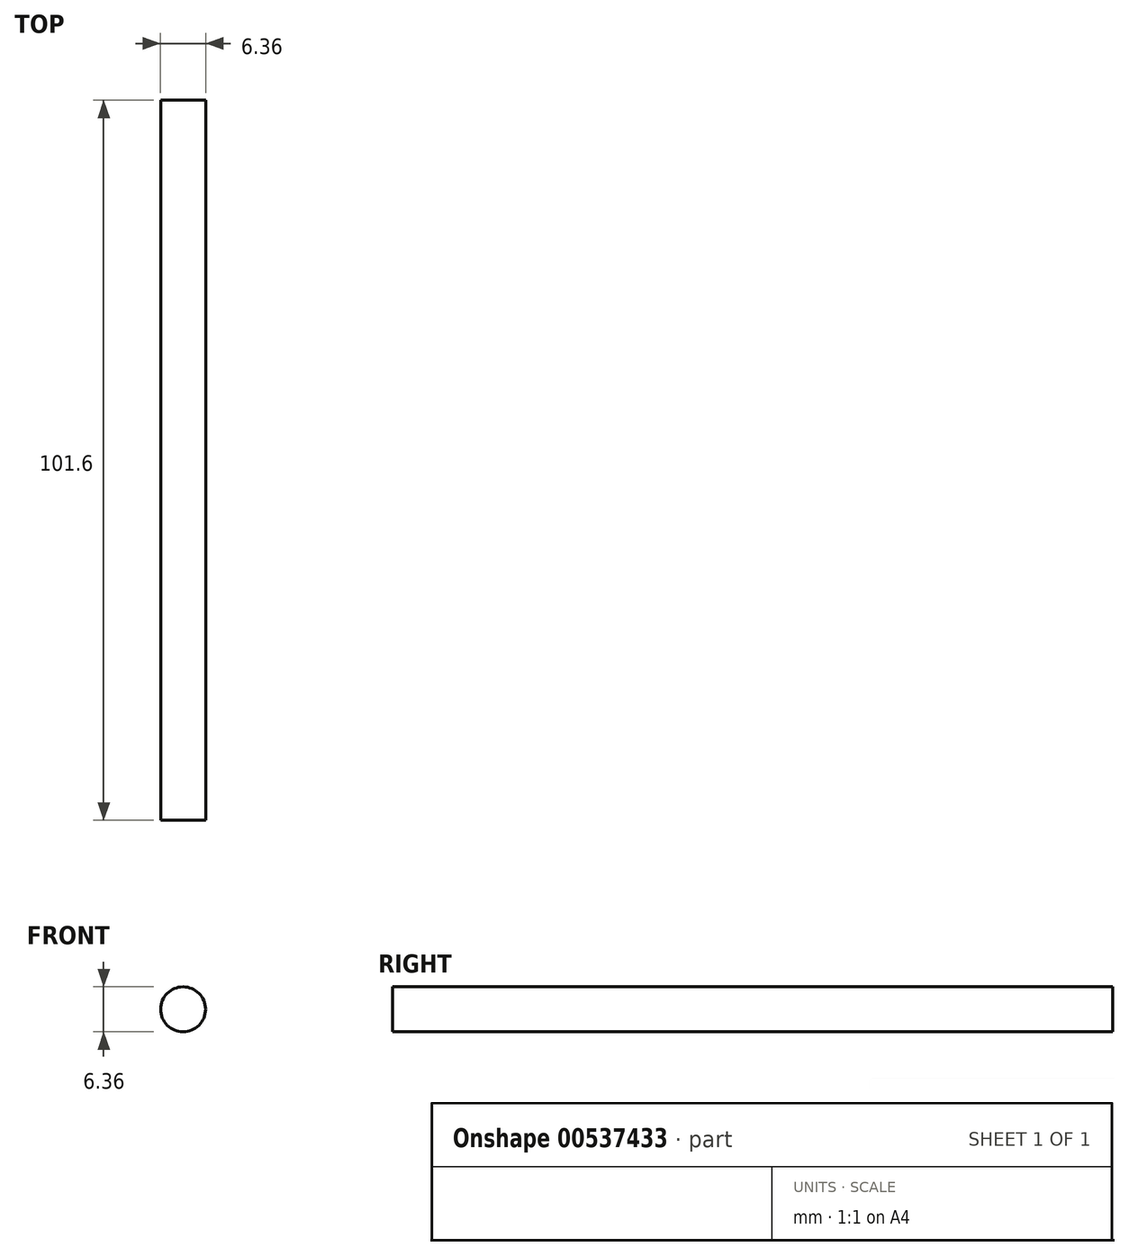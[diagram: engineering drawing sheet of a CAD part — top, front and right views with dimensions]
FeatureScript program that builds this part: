
annotation { "Feature Type Name" : "Feature", "Feature Type Description" : "" }
export const myFeature = defineFeature(function(context is Context, id is Id, definition is map)
    precondition{}
    {
        {
            var Q0;
            Q0=qCreatedBy(makeId("Front.planeOp"),FACE);
            var sketch = newSketch(context, id + "F0", { "sketchPlane" : qUnion([Q0])});
            skCircle(sketch, "E0", {"center": v(0, 0) * mm, "radius": 3.18 * mm});
            skSolve(sketch);
        }
        {
            var Q0;
            Q0 = qSketchRegion(id + "F0", true);
            extrude(context, id + "F1", {"entities" : qUnion([Q0]), "depth" : 101.6 * mm, "offsetDistance" : 25.4 * mm});
        }
    });
